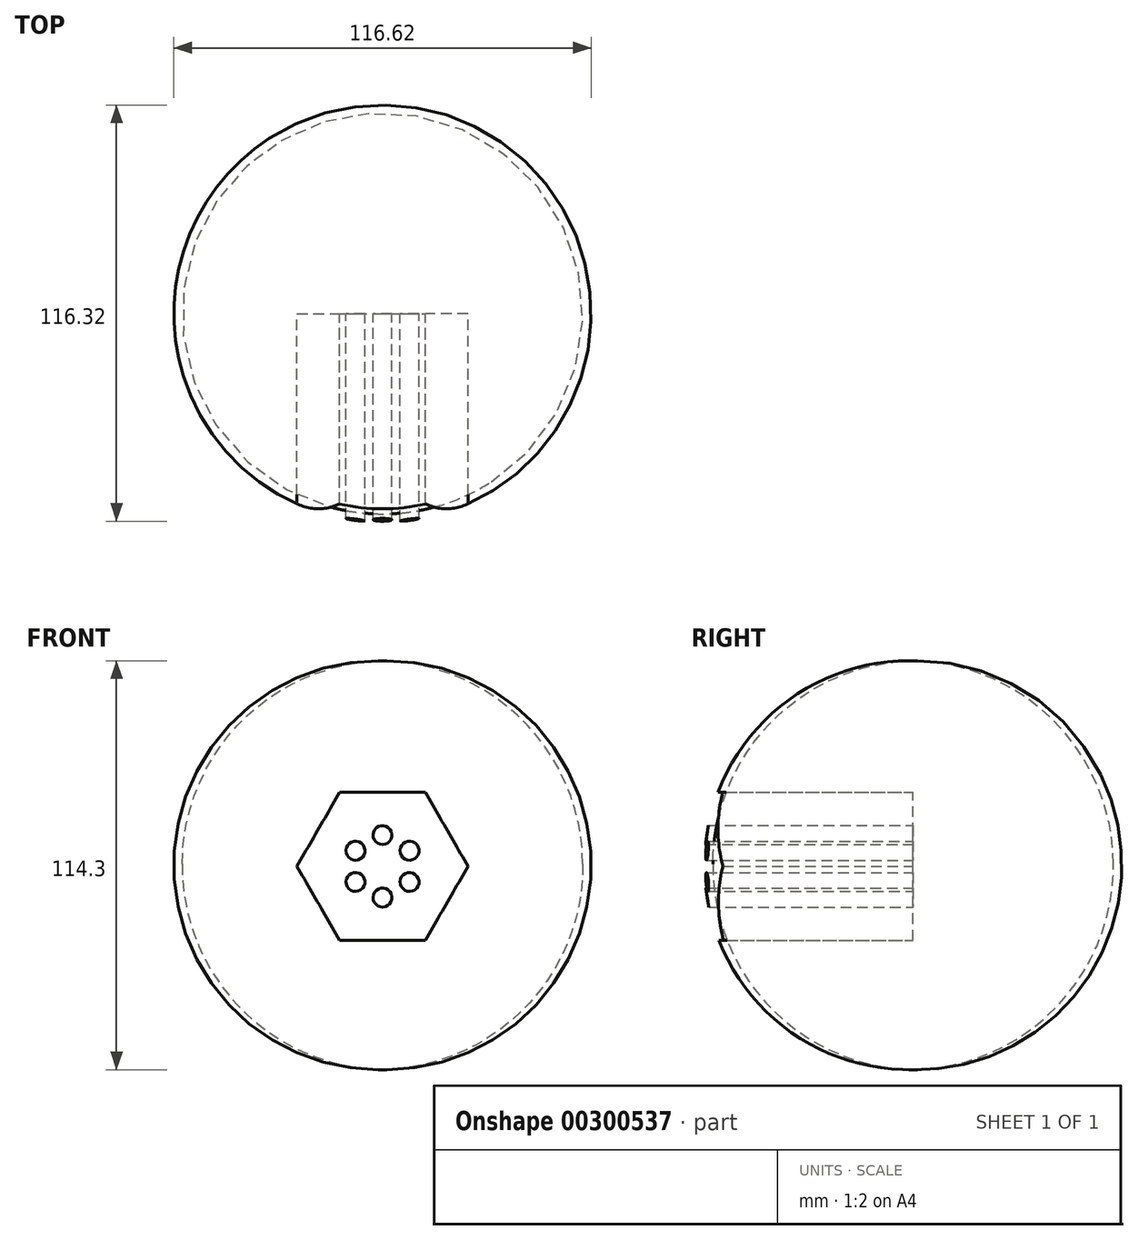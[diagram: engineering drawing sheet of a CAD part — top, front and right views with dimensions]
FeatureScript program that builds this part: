
annotation { "Feature Type Name" : "Feature", "Feature Type Description" : "" }
export const myFeature = defineFeature(function(context is Context, id is Id, definition is map)
    precondition{}
    {
        {
            var Q0;
            Q0=qCreatedBy(makeId("Front.planeOp"),FACE);
            var sketch = newSketch(context, id + "F0", { "sketchPlane" : qUnion([Q0])});
            skArc(sketch, "E0", {"start": v(0, -56.83) * mm, "mid": v(58.3, 0.3) * mm, "end": v(0, 57.45) * mm});
            skLineSegment(sketch, "E1", {"start": v(0, 57.45) * mm, "end": v(0, -56.83) * mm});
            skSolve(sketch);
        }
        {
            var Q0;
            Q0=makeQuery(id+"F0.imprint","IMPRINT",FACE,{"disambiguationData":[TD([[makeQuery(id+"F0.imprint","IMPRINT",EDGE,{"derivedFrom":sQuery(id+"F0.wireOp",EDGE,"E0")}),1.0]])]});
            var Q1;
            Q1=sQuery(id+"F0.wireOp",EDGE,"E1");
            revolve(context, id + "F1", {"entities" : qUnion([Q0]), "axis" : qUnion([Q1]), "revolveType" : RevolveType.FULL});
        }
        {
            var Q0;
            Q0=qCreatedBy(makeId("Front.planeOp"),FACE);
            var sketch = newSketch(context, id + "F2", { "sketchPlane" : qUnion([Q0])});
            skCircle(sketch, "E2.cCircle", {"center": v(0, 0) * mm, "radius": 20.71 * mm, "construction": true});
            skLineSegment(sketch, "E2.0", {"start": v(-11.96, 20.71) * mm, "end": v(11.96, 20.71) * mm});
            skLineSegment(sketch, "E2.1", {"start": v(11.96, 20.71) * mm, "end": v(23.92, 0) * mm});
            skLineSegment(sketch, "E2.2", {"start": v(23.92, 0) * mm, "end": v(11.96, -20.71) * mm});
            skLineSegment(sketch, "E2.3", {"start": v(11.96, -20.71) * mm, "end": v(-11.96, -20.71) * mm});
            skLineSegment(sketch, "E2.4", {"start": v(-11.96, -20.71) * mm, "end": v(-23.92, 0) * mm});
            skLineSegment(sketch, "E2.5", {"start": v(-23.92, 0) * mm, "end": v(-11.96, 20.71) * mm});
            skPoint(sketch, "E2.0.midPoint", {"position": v(0, 20.71) * mm});
            skCircle(sketch, "E3", {"center": v(0, 8.73) * mm, "radius": 2.65 * mm});
            skCircle(sketch, "E4.1.0", {"center": v(-7.56, 4.37) * mm, "radius": 2.65 * mm});
            skCircle(sketch, "E4.2.0", {"center": v(-7.56, -4.37) * mm, "radius": 2.65 * mm});
            skCircle(sketch, "E4.3.0", {"center": v(0, -8.73) * mm, "radius": 2.65 * mm});
            skCircle(sketch, "E4.4.0", {"center": v(7.56, -4.37) * mm, "radius": 2.65 * mm});
            skCircle(sketch, "E4.5.0", {"center": v(7.56, 4.37) * mm, "radius": 2.65 * mm});
            skSolve(sketch);
        }
        {
            var Q0;
            Q0 = qSketchRegion(id + "F2", true);
            extrude(context, id + "F3", {"entities" : qUnion([Q0]), "operationType" : NewBodyOperationType.REMOVE, "depth" : 66.3 * mm});
        }
    });
